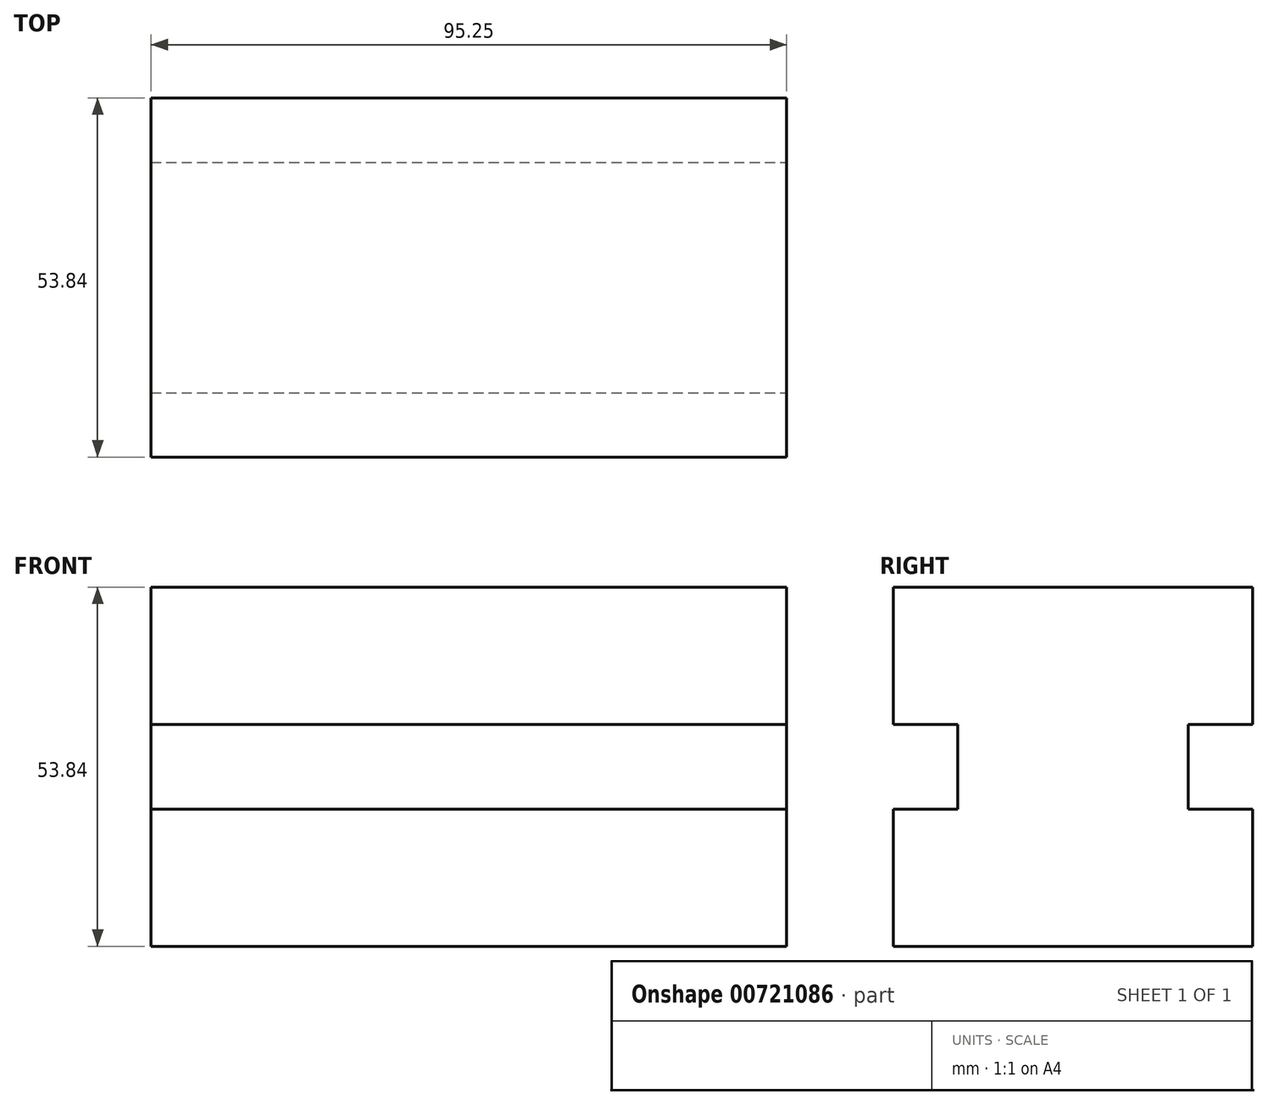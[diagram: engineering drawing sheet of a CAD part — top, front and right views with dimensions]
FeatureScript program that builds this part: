
annotation { "Feature Type Name" : "Feature", "Feature Type Description" : "" }
export const myFeature = defineFeature(function(context is Context, id is Id, definition is map)
    precondition{}
    {
        {
            var Q0;
            Q0=qCreatedBy(makeId("Right.planeOp"),FACE);
            var sketch = newSketch(context, id + "F0", { "sketchPlane" : qUnion([Q0])});
            skLineSegment(sketch, "E0.bottom", {"start": v(26.92, -26.92) * mm, "end": v(-26.92, -26.92) * mm});
            skLineSegment(sketch, "E0.top", {"start": v(26.92, 26.92) * mm, "end": v(-26.92, 26.92) * mm});
            skLineSegment(sketch, "E0.left", {"start": v(26.92, -26.92) * mm, "end": v(26.92, -6.35) * mm});
            skLineSegment(sketch, "E0.right", {"start": v(-26.92, -26.92) * mm, "end": v(-26.92, -6.35) * mm});
            skPoint(sketch, "E0.middle", {"position": v(0, 0) * mm});
            skLineSegment(sketch, "E1.bottom", {"start": v(-26.92, 6.35) * mm, "end": v(-17.27, 6.35) * mm});
            skLineSegment(sketch, "E1.top", {"start": v(-26.92, -6.35) * mm, "end": v(-17.27, -6.35) * mm});
            skLineSegment(sketch, "E1.right", {"start": v(-17.27, 6.35) * mm, "end": v(-17.27, -6.35) * mm});
            skLineSegment(sketch, "E2", {"start": v(0, 46.17) * mm, "end": v(0, -49.66) * mm, "construction": true});
            skPoint(sketch, "E2.startSnap0", {"position": v(0, 26.92) * mm});
            skLineSegment(sketch, "E3.MirrorCS", {"start": v(17.27, 6.35) * mm, "end": v(17.27, -6.35) * mm});
            skLineSegment(sketch, "E4.MirrorCS", {"start": v(26.92, 6.35) * mm, "end": v(17.27, 6.35) * mm});
            skLineSegment(sketch, "E5.MirrorCS", {"start": v(26.92, -6.35) * mm, "end": v(17.27, -6.35) * mm});
            skLineSegment(sketch, "E6.trimOffspring", {"start": v(-26.92, 6.35) * mm, "end": v(-26.92, 26.92) * mm});
            skPoint(sketch, "E7.MirrorCS.end.orphan", {"position": v(26.92, -6.35) * mm});
            skPoint(sketch, "E7.MirrorCS.start.orphan", {"position": v(26.92, 6.35) * mm});
            skLineSegment(sketch, "E8.trimOffspring", {"start": v(26.92, 6.35) * mm, "end": v(26.92, 26.92) * mm});
            skSolve(sketch);
        }
        {
            var Q0;
            Q0=makeQuery(id+"F0.imprint","IMPRINT",FACE,{"disambiguationData":[TD([[makeQuery(id+"F0.imprint","IMPRINT",EDGE,{"derivedFrom":sQuery(id+"F0.wireOp",EDGE,"E0.bottom")}),-1.0]])]});
            extrude(context, id + "F1", {"entities" : qUnion([Q0]), "oppositeDirection" : true, "depth" : 95.25 * mm, "offsetDistance" : 25.4 * mm});
        }
    });
